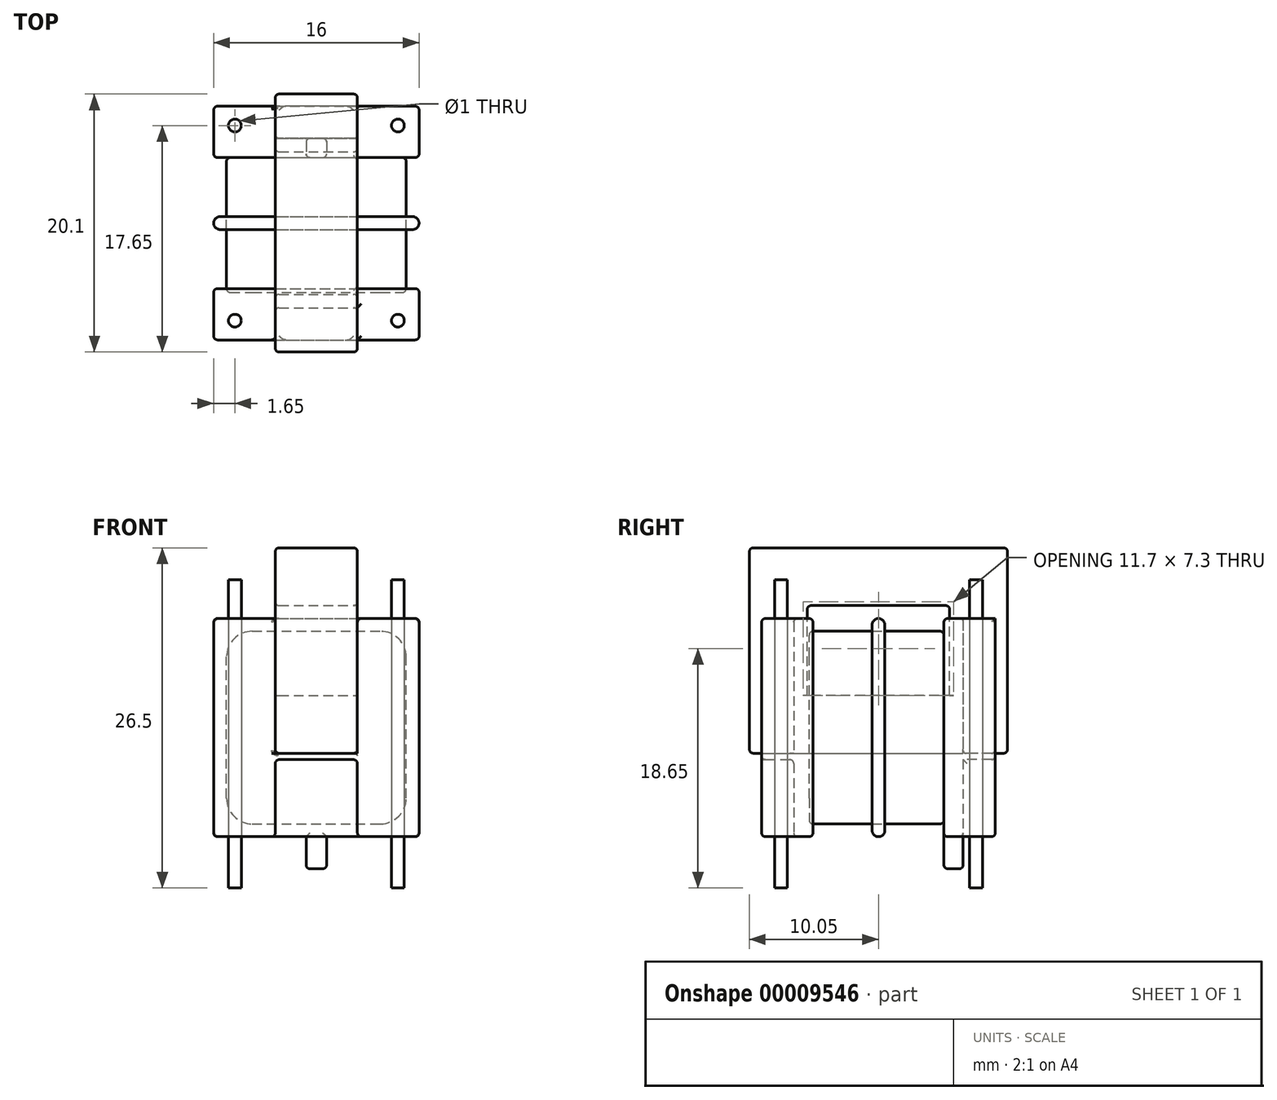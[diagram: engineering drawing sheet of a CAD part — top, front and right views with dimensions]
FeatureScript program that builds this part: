
annotation { "Feature Type Name" : "Feature", "Feature Type Description" : "" }
export const myFeature = defineFeature(function(context is Context, id is Id, definition is map)
    precondition{}
    {
        {
            var Q0;
            Q0=qCreatedBy(makeId("Top.planeOp"),FACE);
            var sketch = newSketch(context, id + "F0", { "sketchPlane" : qUnion([Q0])});
            skCircle(sketch, "E0", {"center": v(-6.35, 7.6) * mm, "radius": 0.5 * mm});
            skCircle(sketch, "E1.0.MirrorC", {"center": v(-6.35, -7.6) * mm, "radius": 0.5 * mm});
            skCircle(sketch, "E2.0.MirrorC", {"center": v(6.35, -7.6) * mm, "radius": 0.5 * mm});
            skCircle(sketch, "E3.0.MirrorC", {"center": v(6.35, 7.6) * mm, "radius": 0.5 * mm});
            skLineSegment(sketch, "E4", {"start": v(-6.35, -7.6) * mm, "end": v(-6.35, 7.6) * mm, "construction": true});
            skLineSegment(sketch, "E5", {"start": v(-6.35, 7.6) * mm, "end": v(6.35, 7.6) * mm, "construction": true});
            skLineSegment(sketch, "E6", {"start": v(6.36, 7.65) * mm, "end": v(6.35, -7.6) * mm, "construction": true});
            skLineSegment(sketch, "E7", {"start": v(-6.35, -7.6) * mm, "end": v(6.35, -7.6) * mm, "construction": true});
            skSolve(sketch);
        }
        {
            var Q0;
            Q0 = qSketchRegion(id + "F0", true);
            extrude(context, id + "F1", {"entities" : qUnion([Q0]), "oppositeDirection" : true, "depth" : 4 * mm});
        }
        {
            var Q0;
            Q0=makeQuery(id+"F0.imprint","IMPRINT",FACE,{"disambiguationData":[TD([[makeQuery(id+"F0.imprint","IMPRINT",EDGE,{"derivedFrom":sQuery(id+"F0.wireOp",EDGE,"E0")}),1.0]])]});
            var sketch = newSketch(context, id + "F2", { "sketchPlane" : qUnion([Q0])});
            skLineSegment(sketch, "E8", {"start": v(0, 0) * mm, "end": v(0, 9.1) * mm, "construction": true});
            skLineSegment(sketch, "E9", {"start": v(0, 0) * mm, "end": v(8, 0) * mm, "construction": true});
            skLineSegment(sketch, "E10.rect.bottom", {"start": v(8, 9.1) * mm, "end": v(-8, 9.1) * mm, "construction": true});
            skLineSegment(sketch, "E10.rect.top", {"start": v(8, -9.1) * mm, "end": v(-8, -9.1) * mm, "construction": true});
            skLineSegment(sketch, "E10.rect.left", {"start": v(8, 9.1) * mm, "end": v(8, -9.1) * mm, "construction": true});
            skLineSegment(sketch, "E10.rect.right", {"start": v(-8, 9.1) * mm, "end": v(-8, -9.1) * mm, "construction": true});
            skPoint(sketch, "E10.rect.middle", {"position": v(0, 0) * mm});
            skLineSegment(sketch, "E11", {"start": v(-8, 5.1) * mm, "end": v(8, 5.1) * mm, "construction": true});
            skLineSegment(sketch, "E12", {"start": v(-3.2, 5.1) * mm, "end": v(-3.2, 9.1) * mm, "construction": true});
            skLineSegment(sketch, "E13.0.MirrorCS", {"start": v(3.2, 5.1) * mm, "end": v(3.2, 9.1) * mm, "construction": true});
            skLineSegment(sketch, "E14", {"start": v(-3.2, 6.6) * mm, "end": v(3.2, 6.6) * mm, "construction": true});
            skLineSegment(sketch, "E15", {"start": v(-8, 5.1) * mm, "end": v(-8, 9.1) * mm});
            skLineSegment(sketch, "E16", {"start": v(-3.2, 9.1) * mm, "end": v(-3.2, 6.6) * mm});
            skLineSegment(sketch, "E17", {"start": v(-8, 9.1) * mm, "end": v(-3.2, 9.1) * mm});
            skLineSegment(sketch, "E18", {"start": v(-3.2, 6.6) * mm, "end": v(3.2, 6.6) * mm});
            skLineSegment(sketch, "E19", {"start": v(3.2, 9.1) * mm, "end": v(3.2, 6.6) * mm});
            skLineSegment(sketch, "E20", {"start": v(3.2, 9.1) * mm, "end": v(8, 9.1) * mm});
            skLineSegment(sketch, "E21", {"start": v(8, 9.1) * mm, "end": v(8, 5.1) * mm});
            skLineSegment(sketch, "E22", {"start": v(-8, 5.1) * mm, "end": v(8, 5.1) * mm});
            skLineSegment(sketch, "E23.0.MirrorCS", {"start": v(-8, -5.1) * mm, "end": v(-8, -9.1) * mm});
            skLineSegment(sketch, "E24.0.MirrorCS", {"start": v(-8, -9.1) * mm, "end": v(-3.2, -9.1) * mm});
            skLineSegment(sketch, "E25.0.MirrorCS", {"start": v(-3.2, -9.1) * mm, "end": v(-3.2, -6.6) * mm});
            skLineSegment(sketch, "E26.0.MirrorCS", {"start": v(-8, -5.1) * mm, "end": v(8, -5.1) * mm});
            skLineSegment(sketch, "E27.0.MirrorCS", {"start": v(-3.2, -6.6) * mm, "end": v(3.2, -6.6) * mm});
            skLineSegment(sketch, "E28.0.MirrorCS", {"start": v(3.2, -9.1) * mm, "end": v(3.2, -6.6) * mm});
            skLineSegment(sketch, "E29.0.MirrorCS", {"start": v(3.2, -9.1) * mm, "end": v(8, -9.1) * mm});
            skLineSegment(sketch, "E30.0.MirrorCS", {"start": v(8, -9.1) * mm, "end": v(8, -5.1) * mm});
            skLineSegment(sketch, "E31", {"start": v(-8, 0.5) * mm, "end": v(8, 0.5) * mm});
            skLineSegment(sketch, "E32.0.MirrorCS", {"start": v(-8, -0.5) * mm, "end": v(8, -0.5) * mm});
            skLineSegment(sketch, "E33", {"start": v(-8, 0.5) * mm, "end": v(-8, -0.5) * mm});
            skLineSegment(sketch, "E34", {"start": v(8, 0.5) * mm, "end": v(8, -0.5) * mm});
            skLineSegment(sketch, "E35", {"start": v(-0.8, 6.6) * mm, "end": v(-0.8, 5.1) * mm});
            skLineSegment(sketch, "E36.0.MirrorCS", {"start": v(0.8, 6.6) * mm, "end": v(0.8, 5.1) * mm});
            skSolve(sketch);
        }
        {
            var Q0;
            Q0=makeQuery(id+"F2.imprint","IMPRINT",FACE,{"disambiguationData":[TD([[makeQuery(id+"F2.imprint","IMPRINT",EDGE,{"derivedFrom":sQuery(id+"F2.wireOp",EDGE,"E15")}),-1.0]])]});
            var Q1;
            Q1=makeQuery(id+"F2.imprint","IMPRINT",FACE,{"disambiguationData":[TD([[makeQuery(id+"F2.imprint","IMPRINT",EDGE,{"derivedFrom":sQuery(id+"F2.wireOp",EDGE,"E23.0.MirrorCS")}),1.0]])]});
            var Q2;
            Q2=makeQuery(id+"F2.imprint","IMPRINT",FACE,{"disambiguationData":[TD([[makeQuery(id+"F2.imprint","IMPRINT",EDGE,{"derivedFrom":sQuery(id+"F2.wireOp",EDGE,"E31")}),-1.0]])]});
            var Q3;
            {var subQ1=sQuery(id+"F2.wireOp",EDGE,"E35");Q3=makeQuery(id+"F2.imprint","IMPRINT",FACE,{"disambiguationData":[TD([[makeQuery(id+"F2.imprint","IMPRINT",EDGE,{"derivedFrom":subQ1}),1.0]])]});}
            var Q4;
            {var subQ3=sQuery(id+"F2.wireOp",EDGE,"E19");Q4=makeQuery(id+"F2.imprint","IMPRINT",FACE,{"disambiguationData":[TD([[makeQuery(id+"F2.imprint","IMPRINT",EDGE,{"derivedFrom":subQ3}),1.0]])]});}
            extrude(context, id + "F3", {"entities" : qUnion([Q0, Q1, Q2, Q3, Q4]), "depth" : 17 * mm});
        }
        {
            var Q0;
            {var subQ1=sQuery(id+"F2.wireOp",EDGE,"E35");Q0=makeQuery(id+"F2.imprint","IMPRINT",FACE,{"disambiguationData":[TD([[makeQuery(id+"F2.imprint","IMPRINT",EDGE,{"derivedFrom":subQ1}),1.0]])]});}
            extrude(context, id + "F4", {"entities" : qUnion([Q0]), "operationType" : NewBodyOperationType.ADD, "oppositeDirection" : true, "depth" : 2.5 * mm});
        }
        {
            var Q0;
            {var subQ0=sQuery(id+"F2.wireOp",EDGE,"E18");Q0=makeQuery(id+"F4.boolean.opBoolean","MERGE",FACE,{"derivedFrom":[makeQuery(id+"F3.opExtrude","SWEPT_FACE",FACE,{"disambiguationData":[OSD([subQ0])]}),makeQuery(id+"F4.opExtrude","SWEPT_FACE",FACE,{"disambiguationData":[OSD([subQ0])]})]});}
            var sketch = newSketch(context, id + "F5", { "sketchPlane" : qUnion([Q0])});
            skLineSegment(sketch, "E37", {"start": v(0, 0) * mm, "end": v(0, 6) * mm, "construction": true});
            skLineSegment(sketch, "E38", {"start": v(-3.2, 6) * mm, "end": v(3.2, 6) * mm});
            skLineSegment(sketch, "E39", {"start": v(-3.2, 6.5) * mm, "end": v(3.2, 6.5) * mm});
            skLineSegment(sketch, "E40", {"start": v(-3.2, 6.5) * mm, "end": v(-3.2, 6) * mm});
            skLineSegment(sketch, "E41", {"start": v(3.2, 6.5) * mm, "end": v(3.2, 6) * mm});
            skSolve(sketch);
        }
        {
            var Q0;
            Q0 = qSketchRegion(id + "F5", true);
            extrude(context, id + "F6", {"entities" : qUnion([Q0]), "operationType" : NewBodyOperationType.ADD, "depth" : 2.5 * mm});
        }
        {
            var Q0;
            Q0=makeQuery(id+"F3.opExtrude","SWEPT_FACE",FACE,{"disambiguationData":[OSD([sQuery(id+"F2.wireOp",EDGE,"E27.0.MirrorCS")])]});
            var sketch = newSketch(context, id + "F7", { "sketchPlane" : qUnion([Q0])});
            skLineSegment(sketch, "E42", {"start": v(-3.2, 6) * mm, "end": v(3.2, 6) * mm});
            skLineSegment(sketch, "E43", {"start": v(-3.2, 6.5) * mm, "end": v(3.2, 6.5) * mm});
            skLineSegment(sketch, "E44", {"start": v(3.2, 6.5) * mm, "end": v(3.2, 6) * mm});
            skLineSegment(sketch, "E45", {"start": v(-3.2, 6) * mm, "end": v(-3.2, 6.5) * mm});
            skSolve(sketch);
        }
        {
            var Q0;
            Q0=makeQuery(id+"F7.imprint","IMPRINT",FACE,{"disambiguationData":[TD([[makeQuery(id+"F7.imprint","IMPRINT",EDGE,{"derivedFrom":sQuery(id+"F7.wireOp",EDGE,"E42")}),1.0]])]});
            extrude(context, id + "F8", {"entities" : qUnion([Q0]), "operationType" : NewBodyOperationType.ADD, "depth" : 2.5 * mm});
        }
        {
            var Q0;
            {var subQ0=sQuery(id+"F2.wireOp",EDGE,"E19");var subQ1=sQuery(id+"F5.wireOp",EDGE,"E39");Q0=makeQuery(id+"F6.boolean.opBoolean","SPLIT",FACE,{"disambiguationData":[TD([makeQuery(id+"F6.opExtrude","SWEPT_FACE",FACE,{"disambiguationData":[OSD([subQ1])]})])],"derivedFrom":makeQuery(id+"F3.opExtrude","SWEPT_FACE",FACE,{"disambiguationData":[OSD([subQ0])]})});}
            var sketch = newSketch(context, id + "F9", { "sketchPlane" : qUnion([Q0])});
            skLineSegment(sketch, "E46", {"start": v(0, 6.5) * mm, "end": v(-10.05, 6.5) * mm});
            skLineSegment(sketch, "E47", {"start": v(-10.05, 6.5) * mm, "end": v(-10.05, 22.5) * mm});
            skLineSegment(sketch, "E48", {"start": v(-10.05, 22.5) * mm, "end": v(0, 22.5) * mm});
            skLineSegment(sketch, "E49.0.MirrorCS", {"start": v(10.05, 6.5) * mm, "end": v(10.05, 22.5) * mm});
            skLineSegment(sketch, "E49.1.MirrorCS", {"start": v(0, 6.5) * mm, "end": v(10.05, 6.5) * mm});
            skLineSegment(sketch, "E49.2.MirrorCS", {"start": v(10.05, 22.5) * mm, "end": v(0, 22.5) * mm});
            skLineSegment(sketch, "E50.0", {"start": v(-5.55, 18) * mm, "end": v(0, 18) * mm});
            skLineSegment(sketch, "E50.1", {"start": v(-5.55, 11) * mm, "end": v(-5.55, 18) * mm});
            skLineSegment(sketch, "E50.2", {"start": v(0, 11) * mm, "end": v(-5.55, 11) * mm});
            skLineSegment(sketch, "E50.3", {"start": v(0, 11) * mm, "end": v(5.55, 11) * mm});
            skLineSegment(sketch, "E50.4", {"start": v(5.55, 11) * mm, "end": v(5.55, 18) * mm});
            skLineSegment(sketch, "E50.5", {"start": v(5.55, 18) * mm, "end": v(0, 18) * mm});
            skSolve(sketch);
        }
        {
            var Q0;
            {var subQ11=sQuery(id+"F9.wireOp",EDGE,"E47");Q0=makeQuery(id+"F9.imprint","IMPRINT",FACE,{"disambiguationData":[TD([[makeQuery(id+"F9.imprint","IMPRINT",EDGE,{"derivedFrom":subQ11}),-1.0]])]});}
            extrude(context, id + "F10", {"entities" : qUnion([Q0]), "depth" : 6.4 * mm});
        }
        {
            var Q0;
            {var subQ0=sQuery(id+"F2.wireOp",EDGE,"E22");Q0=makeQuery(id+"F4.boolean.opBoolean","MERGE",FACE,{"derivedFrom":[makeQuery(id+"F3.opExtrude","SWEPT_FACE",FACE,{"disambiguationData":[OSD([subQ0])]}),makeQuery(id+"F4.opExtrude","SWEPT_FACE",FACE,{"disambiguationData":[OSD([subQ0])]})]});}
            var sketch = newSketch(context, id + "F11", { "sketchPlane" : qUnion([Q0])});
            skLineSegment(sketch, "E51.0", {"start": v(-7, 3) * mm, "end": v(-7, 14) * mm});
            skLineSegment(sketch, "E51.1", {"start": v(-5, 1) * mm, "end": v(5, 1) * mm});
            skLineSegment(sketch, "E51.2", {"start": v(7, 3) * mm, "end": v(7, 14) * mm});
            skLineSegment(sketch, "E51.3", {"start": v(-5, 16) * mm, "end": v(5, 16) * mm});
            skPoint(sketch, "E52.visualSharp", {"position": v(-7, 16) * mm});
            skArc(sketch, "E52.filletArc", {"start": v(-5, 16) * mm, "mid": v(-6.41, 15.41) * mm, "end": v(-7, 14) * mm});
            skPoint(sketch, "E53.visualSharp", {"position": v(7, 16) * mm});
            skArc(sketch, "E53.filletArc", {"start": v(7, 14) * mm, "mid": v(6.41, 15.41) * mm, "end": v(5, 16) * mm});
            skPoint(sketch, "E54.visualSharp", {"position": v(7, 1) * mm});
            skArc(sketch, "E54.filletArc", {"start": v(5, 1) * mm, "mid": v(6.41, 1.59) * mm, "end": v(7, 3) * mm});
            skPoint(sketch, "E55.visualSharp", {"position": v(-7, 1) * mm});
            skArc(sketch, "E55.filletArc", {"start": v(-7, 3) * mm, "mid": v(-6.41, 1.59) * mm, "end": v(-5, 1) * mm});
            skPoint(sketch, "E56.visualSharp", {"position": v(-8, 0) * mm});
            skSolve(sketch);
        }
        {
            var Q0;
            Q0=makeQuery(id+"F11.imprint","IMPRINT",FACE,{"disambiguationData":[TD([[makeQuery(id+"F11.imprint","IMPRINT",EDGE,{"derivedFrom":sQuery(id+"F11.wireOp",EDGE,"E51.0")}),-1.0]])]});
            extrude(context, id + "F12", {"entities" : qUnion([Q0]), "depth" : 10.5 * mm});
        }
        {
            var Q0;
            Q0=makeQuery(id+"F12.opExtrude","SWEPT_FACE",FACE,{"disambiguationData":[OSD([sQuery(id+"F11.wireOp",EDGE,"E51.0")])]});
            var Q1;
            Q1=makeQuery(id+"F3.opExtrude","SWEPT_EDGE",EDGE,{"disambiguationData":[OSD([sQuery(id+"F2.wireOp",EDGE,"E29.0.MirrorCS"),sQuery(id+"F2.wireOp",EDGE,"E30.0.MirrorCS")])]});
            var Q2;
            Q2=makeQuery(id+"F3.opExtrude","CAP_EDGE",EDGE,{"disambiguationData":[OSD([sQuery(id+"F2.wireOp",EDGE,"E29.0.MirrorCS")])],"isStart":false});
            var Q3;
            Q3=makeQuery(id+"F3.opExtrude","CAP_EDGE",EDGE,{"disambiguationData":[OSD([sQuery(id+"F2.wireOp",EDGE,"E30.0.MirrorCS")])],"isStart":false});
            var Q4;
            Q4=makeQuery(id+"F3.opExtrude","SWEPT_EDGE",EDGE,{"disambiguationData":[OSD([sQuery(id+"F2.wireOp",EDGE,"E26.0.MirrorCS"),sQuery(id+"F2.wireOp",EDGE,"E30.0.MirrorCS")])]});
            var Q5;
            Q5=makeQuery(id+"F3.opExtrude","CAP_EDGE",EDGE,{"disambiguationData":[OSD([sQuery(id+"F2.wireOp",EDGE,"E26.0.MirrorCS")])],"isStart":false});
            var Q6;
            {var subQ0=sQuery(id+"F2.wireOp",EDGE,"E28.0.MirrorCS");var subQ1=sQuery(id+"F2.wireOp",EDGE,"E29.0.MirrorCS");var subQ2=sQuery(id+"F7.wireOp",EDGE,"E42");Q6=makeQuery(id+"F8.boolean.opBoolean","SPLIT",EDGE,{"disambiguationData":[TD([makeQuery(id+"F8.opExtrude","SWEPT_FACE",FACE,{"disambiguationData":[OSD([subQ2])]})])],"derivedFrom":makeQuery(id+"F3.opExtrude","SWEPT_EDGE",EDGE,{"disambiguationData":[OSD([subQ0,subQ1])]})});}
            var Q7;
            Q7=makeQuery(id+"F3.opExtrude","CAP_EDGE",EDGE,{"disambiguationData":[OSD([sQuery(id+"F2.wireOp",EDGE,"E29.0.MirrorCS")])],"isStart":true});
            var Q8;
            {var subQ0=sQuery(id+"F2.wireOp",EDGE,"E24.0.MirrorCS");var subQ1=sQuery(id+"F2.wireOp",EDGE,"E25.0.MirrorCS");var subQ2=sQuery(id+"F7.wireOp",EDGE,"E43");Q8=makeQuery(id+"F8.boolean.opBoolean","SPLIT",EDGE,{"disambiguationData":[TD([makeQuery(id+"F8.opExtrude","SWEPT_FACE",FACE,{"disambiguationData":[OSD([subQ2])]})])],"derivedFrom":makeQuery(id+"F3.opExtrude","SWEPT_EDGE",EDGE,{"disambiguationData":[OSD([subQ0,subQ1])]})});}
            var Q9;
            Q9=makeQuery(id+"F3.opExtrude","CAP_EDGE",EDGE,{"disambiguationData":[OSD([sQuery(id+"F2.wireOp",EDGE,"E25.0.MirrorCS")])],"isStart":false});
            var Q10;
            Q10=makeQuery(id+"F3.opExtrude","CAP_EDGE",EDGE,{"disambiguationData":[OSD([sQuery(id+"F2.wireOp",EDGE,"E27.0.MirrorCS")])],"isStart":false});
            var Q11;
            Q11=makeQuery(id+"F3.opExtrude","SWEPT_EDGE",EDGE,{"disambiguationData":[OSD([sQuery(id+"F2.wireOp",EDGE,"E23.0.MirrorCS"),sQuery(id+"F2.wireOp",EDGE,"E24.0.MirrorCS")])]});
            var Q12;
            Q12=makeQuery(id+"F3.opExtrude","CAP_EDGE",EDGE,{"disambiguationData":[OSD([sQuery(id+"F2.wireOp",EDGE,"E23.0.MirrorCS")])],"isStart":false});
            var Q13;
            Q13=makeQuery(id+"F3.opExtrude","CAP_EDGE",EDGE,{"disambiguationData":[OSD([sQuery(id+"F2.wireOp",EDGE,"E24.0.MirrorCS")])],"isStart":false});
            var Q14;
            Q14=makeQuery(id+"F3.opExtrude","SWEPT_EDGE",EDGE,{"disambiguationData":[OSD([sQuery(id+"F2.wireOp",EDGE,"E23.0.MirrorCS"),sQuery(id+"F2.wireOp",EDGE,"E26.0.MirrorCS")])]});
            var Q15;
            Q15=makeQuery(id+"F3.opExtrude","CAP_EDGE",EDGE,{"disambiguationData":[OSD([sQuery(id+"F2.wireOp",EDGE,"E23.0.MirrorCS")])],"isStart":true});
            var Q16;
            Q16=makeQuery(id+"F3.opExtrude","CAP_EDGE",EDGE,{"disambiguationData":[OSD([sQuery(id+"F2.wireOp",EDGE,"E26.0.MirrorCS")])],"isStart":true});
            var Q17;
            Q17=makeQuery(id+"F3.opExtrude","CAP_EDGE",EDGE,{"disambiguationData":[OSD([sQuery(id+"F2.wireOp",EDGE,"E27.0.MirrorCS")])],"isStart":true});
            var Q18;
            Q18=makeQuery(id+"F3.opExtrude","CAP_EDGE",EDGE,{"disambiguationData":[OSD([sQuery(id+"F2.wireOp",EDGE,"E25.0.MirrorCS")])],"isStart":true});
            var Q19;
            Q19=makeQuery(id+"F3.opExtrude","CAP_EDGE",EDGE,{"disambiguationData":[OSD([sQuery(id+"F2.wireOp",EDGE,"E24.0.MirrorCS")])],"isStart":true});
            var Q20;
            Q20=makeQuery(id+"F3.opExtrude","CAP_EDGE",EDGE,{"disambiguationData":[OSD([sQuery(id+"F2.wireOp",EDGE,"E28.0.MirrorCS")])],"isStart":true});
            var Q21;
            Q21=makeQuery(id+"F3.opExtrude","CAP_EDGE",EDGE,{"disambiguationData":[OSD([sQuery(id+"F2.wireOp",EDGE,"E30.0.MirrorCS")])],"isStart":true});
            var Q22;
            Q22=makeQuery(id+"F3.opExtrude","CAP_EDGE",EDGE,{"disambiguationData":[OSD([sQuery(id+"F2.wireOp",EDGE,"E28.0.MirrorCS")])],"isStart":false});
            var Q23;
            {var subQ0=sQuery(id+"F2.wireOp",EDGE,"E22");var subQ1=sQuery(id+"F2.wireOp",EDGE,"E21");Q23=makeQuery(id+"F4.boolean.opBoolean","SPLIT",EDGE,{"disambiguationData":[TD([makeQuery(id+"F3.opExtrude","SWEPT_FACE",FACE,{"disambiguationData":[OSD([subQ1])]})])],"derivedFrom":makeQuery(id+"F3.opExtrude","CAP_EDGE",EDGE,{"disambiguationData":[OSD([subQ0])],"isStart":true})});}
            var Q24;
            Q24=makeQuery(id+"F3.opExtrude","CAP_EDGE",EDGE,{"disambiguationData":[OSD([sQuery(id+"F2.wireOp",EDGE,"E21")])],"isStart":true});
            var Q25;
            Q25=makeQuery(id+"F3.opExtrude","CAP_EDGE",EDGE,{"disambiguationData":[OSD([sQuery(id+"F2.wireOp",EDGE,"E20")])],"isStart":true});
            var Q26;
            Q26=makeQuery(id+"F3.opExtrude","CAP_EDGE",EDGE,{"disambiguationData":[OSD([sQuery(id+"F2.wireOp",EDGE,"E19")])],"isStart":true});
            var Q27;
            {var subQ0=sQuery(id+"F2.wireOp",EDGE,"E18");var subQ1=sQuery(id+"F2.wireOp",EDGE,"E19");Q27=makeQuery(id+"F4.boolean.opBoolean","SPLIT",EDGE,{"disambiguationData":[TD([makeQuery(id+"F3.opExtrude","SWEPT_FACE",FACE,{"disambiguationData":[OSD([subQ1])]})])],"derivedFrom":makeQuery(id+"F3.opExtrude","CAP_EDGE",EDGE,{"disambiguationData":[OSD([subQ0])],"isStart":true})});}
            var Q28;
            Q28=makeQuery(id+"F4.opExtrude","SWEPT_EDGE",EDGE,{"disambiguationData":[OSD([sQuery(id+"F2.wireOp",EDGE,"E18"),sQuery(id+"F2.wireOp",EDGE,"E36.0.MirrorCS")])]});
            var Q29;
            Q29=makeQuery(id+"F4.opExtrude","CAP_EDGE",EDGE,{"disambiguationData":[OSD([sQuery(id+"F2.wireOp",EDGE,"E18")])],"isStart":false});
            var Q30;
            Q30=makeQuery(id+"F4.opExtrude","SWEPT_EDGE",EDGE,{"disambiguationData":[OSD([sQuery(id+"F2.wireOp",EDGE,"E18"),sQuery(id+"F2.wireOp",EDGE,"E35")])]});
            var Q31;
            {var subQ0=sQuery(id+"F2.wireOp",EDGE,"E18");var subQ1=sQuery(id+"F2.wireOp",EDGE,"E16");Q31=makeQuery(id+"F4.boolean.opBoolean","SPLIT",EDGE,{"disambiguationData":[TD([makeQuery(id+"F3.opExtrude","SWEPT_FACE",FACE,{"disambiguationData":[OSD([subQ1])]})])],"derivedFrom":makeQuery(id+"F3.opExtrude","CAP_EDGE",EDGE,{"disambiguationData":[OSD([subQ0])],"isStart":true})});}
            var Q32;
            {var subQ0=sQuery(id+"F2.wireOp",EDGE,"E18");var subQ1=sQuery(id+"F2.wireOp",EDGE,"E16");Q32=makeQuery(id+"F4.boolean.opBoolean","SPLIT",EDGE,{"disambiguationData":[TD([makeQuery(id+"F3.opExtrude","SWEPT_FACE",FACE,{"disambiguationData":[OSD([subQ1])]})])],"derivedFrom":makeQuery(id+"F3.opExtrude","CAP_EDGE",EDGE,{"disambiguationData":[OSD([subQ0])],"isStart":true})});}
            var Q33;
            Q33=makeQuery(id+"F3.opExtrude","CAP_EDGE",EDGE,{"disambiguationData":[OSD([sQuery(id+"F2.wireOp",EDGE,"E16")])],"isStart":true});
            var Q34;
            Q34=makeQuery(id+"F3.opExtrude","CAP_EDGE",EDGE,{"disambiguationData":[OSD([sQuery(id+"F2.wireOp",EDGE,"E17")])],"isStart":true});
            var Q35;
            Q35=makeQuery(id+"F3.opExtrude","CAP_EDGE",EDGE,{"disambiguationData":[OSD([sQuery(id+"F2.wireOp",EDGE,"E15")])],"isStart":true});
            var Q36;
            {var subQ0=sQuery(id+"F2.wireOp",EDGE,"E22");var subQ1=sQuery(id+"F2.wireOp",EDGE,"E15");Q36=makeQuery(id+"F4.boolean.opBoolean","SPLIT",EDGE,{"disambiguationData":[TD([makeQuery(id+"F3.opExtrude","SWEPT_FACE",FACE,{"disambiguationData":[OSD([subQ1])]})])],"derivedFrom":makeQuery(id+"F3.opExtrude","CAP_EDGE",EDGE,{"disambiguationData":[OSD([subQ0])],"isStart":true})});}
            var Q37;
            Q37=makeQuery(id+"F4.opExtrude","SWEPT_EDGE",EDGE,{"disambiguationData":[OSD([sQuery(id+"F2.wireOp",EDGE,"E22"),sQuery(id+"F2.wireOp",EDGE,"E35")])]});
            var Q38;
            Q38=makeQuery(id+"F4.opExtrude","CAP_EDGE",EDGE,{"disambiguationData":[OSD([sQuery(id+"F2.wireOp",EDGE,"E22")])],"isStart":false});
            var Q39;
            Q39=makeQuery(id+"F4.opExtrude","SWEPT_EDGE",EDGE,{"disambiguationData":[OSD([sQuery(id+"F2.wireOp",EDGE,"E22"),sQuery(id+"F2.wireOp",EDGE,"E36.0.MirrorCS")])]});
            var Q40;
            Q40=makeQuery(id+"F4.opExtrude","CAP_EDGE",EDGE,{"disambiguationData":[OSD([sQuery(id+"F2.wireOp",EDGE,"E35")])],"isStart":false});
            var Q41;
            Q41=makeQuery(id+"F4.opExtrude","CAP_EDGE",EDGE,{"disambiguationData":[OSD([sQuery(id+"F2.wireOp",EDGE,"E36.0.MirrorCS")])],"isStart":false});
            var Q42;
            {var subQ0=sQuery(id+"F2.wireOp",EDGE,"E16");var subQ1=sQuery(id+"F2.wireOp",EDGE,"E18");Q42=makeQuery(id+"F6.boolean.opBoolean","SPLIT",EDGE,{"disambiguationData":[TD([makeQuery(id+"F6.opExtrude","SWEPT_FACE",FACE,{"disambiguationData":[OSD([sQuery(id+"F5.wireOp",EDGE,"E38")])]})])],"derivedFrom":makeQuery(id+"F3.opExtrude","SWEPT_EDGE",EDGE,{"disambiguationData":[OSD([subQ0,subQ1])]})});}
            var Q43;
            {var subQ0=sQuery(id+"F2.wireOp",EDGE,"E16");var subQ1=sQuery(id+"F2.wireOp",EDGE,"E17");var subQ2=sQuery(id+"F5.wireOp",EDGE,"E38");Q43=makeQuery(id+"F6.boolean.opBoolean","SPLIT",EDGE,{"disambiguationData":[TD([makeQuery(id+"F6.opExtrude","SWEPT_FACE",FACE,{"disambiguationData":[OSD([subQ2])]})])],"derivedFrom":makeQuery(id+"F3.opExtrude","SWEPT_EDGE",EDGE,{"disambiguationData":[OSD([subQ0,subQ1])]})});}
            var Q44;
            Q44=makeQuery(id+"F6.opExtrude","CAP_EDGE",EDGE,{"disambiguationData":[OSD([sQuery(id+"F5.wireOp",EDGE,"E38")])],"isStart":true});
            var Q45;
            Q45=makeQuery(id+"F6.opExtrude","SWEPT_EDGE",EDGE,{"disambiguationData":[OSD([sQuery(id+"F2.wireOp",EDGE,"E16"),sQuery(id+"F2.wireOp",EDGE,"E18"),sQuery(id+"F5.wireOp",EDGE,"E38"),sQuery(id+"F5.wireOp",EDGE,"E41")])]});
            var Q46;
            {var subQ0=sQuery(id+"F2.wireOp",EDGE,"E18");var subQ1=sQuery(id+"F2.wireOp",EDGE,"E19");Q46=makeQuery(id+"F6.boolean.opBoolean","SPLIT",EDGE,{"disambiguationData":[TD([makeQuery(id+"F6.opExtrude","SWEPT_FACE",FACE,{"disambiguationData":[OSD([sQuery(id+"F5.wireOp",EDGE,"E38")])]})])],"derivedFrom":makeQuery(id+"F3.opExtrude","SWEPT_EDGE",EDGE,{"disambiguationData":[OSD([subQ0,subQ1])]})});}
            var Q47;
            {var subQ0=sQuery(id+"F2.wireOp",EDGE,"E19");var subQ1=sQuery(id+"F2.wireOp",EDGE,"E20");var subQ2=sQuery(id+"F5.wireOp",EDGE,"E38");Q47=makeQuery(id+"F6.boolean.opBoolean","SPLIT",EDGE,{"disambiguationData":[TD([makeQuery(id+"F6.opExtrude","SWEPT_FACE",FACE,{"disambiguationData":[OSD([subQ2])]})])],"derivedFrom":makeQuery(id+"F3.opExtrude","SWEPT_EDGE",EDGE,{"disambiguationData":[OSD([subQ0,subQ1])]})});}
            var Q48;
            Q48=makeQuery(id+"F6.opExtrude","SWEPT_EDGE",EDGE,{"disambiguationData":[OSD([sQuery(id+"F2.wireOp",EDGE,"E18"),sQuery(id+"F2.wireOp",EDGE,"E19"),sQuery(id+"F5.wireOp",EDGE,"E38"),sQuery(id+"F5.wireOp",EDGE,"E40")])]});
            var Q49;
            Q49=makeQuery(id+"F3.opExtrude","SWEPT_EDGE",EDGE,{"disambiguationData":[OSD([sQuery(id+"F2.wireOp",EDGE,"E20"),sQuery(id+"F2.wireOp",EDGE,"E21")])]});
            var Q50;
            Q50=makeQuery(id+"F3.opExtrude","SWEPT_EDGE",EDGE,{"disambiguationData":[OSD([sQuery(id+"F2.wireOp",EDGE,"E21"),sQuery(id+"F2.wireOp",EDGE,"E22")])]});
            var Q51;
            Q51=makeQuery(id+"F3.opExtrude","CAP_EDGE",EDGE,{"disambiguationData":[OSD([sQuery(id+"F2.wireOp",EDGE,"E21")])],"isStart":false});
            var Q52;
            Q52=makeQuery(id+"F3.opExtrude","CAP_EDGE",EDGE,{"disambiguationData":[OSD([sQuery(id+"F2.wireOp",EDGE,"E20")])],"isStart":false});
            var Q53;
            Q53=makeQuery(id+"F3.opExtrude","CAP_EDGE",EDGE,{"disambiguationData":[OSD([sQuery(id+"F2.wireOp",EDGE,"E22")])],"isStart":false});
            var Q54;
            {var subQ0=sQuery(id+"F2.wireOp",EDGE,"E24.0.MirrorCS");var subQ1=sQuery(id+"F2.wireOp",EDGE,"E25.0.MirrorCS");var subQ2=sQuery(id+"F7.wireOp",EDGE,"E42");Q54=makeQuery(id+"F8.boolean.opBoolean","SPLIT",EDGE,{"disambiguationData":[TD([makeQuery(id+"F8.opExtrude","SWEPT_FACE",FACE,{"disambiguationData":[OSD([subQ2])]})])],"derivedFrom":makeQuery(id+"F3.opExtrude","SWEPT_EDGE",EDGE,{"disambiguationData":[OSD([subQ0,subQ1])]})});}
            var Q55;
            {var subQ0=sQuery(id+"F2.wireOp",EDGE,"E25.0.MirrorCS");var subQ1=sQuery(id+"F2.wireOp",EDGE,"E27.0.MirrorCS");Q55=makeQuery(id+"F8.boolean.opBoolean","SPLIT",EDGE,{"disambiguationData":[TD([makeQuery(id+"F8.opExtrude","SWEPT_FACE",FACE,{"disambiguationData":[OSD([sQuery(id+"F7.wireOp",EDGE,"E42")])]})])],"derivedFrom":makeQuery(id+"F3.opExtrude","SWEPT_EDGE",EDGE,{"disambiguationData":[OSD([subQ0,subQ1])]})});}
            var Q56;
            Q56=makeQuery(id+"F8.opExtrude","SWEPT_EDGE",EDGE,{"disambiguationData":[OSD([sQuery(id+"F2.wireOp",EDGE,"E25.0.MirrorCS"),sQuery(id+"F2.wireOp",EDGE,"E27.0.MirrorCS"),sQuery(id+"F7.wireOp",EDGE,"E42"),sQuery(id+"F7.wireOp",EDGE,"E45")])]});
            var Q57;
            Q57=makeQuery(id+"F8.opExtrude","CAP_EDGE",EDGE,{"disambiguationData":[OSD([sQuery(id+"F7.wireOp",EDGE,"E42")])],"isStart":true});
            var Q58;
            Q58=makeQuery(id+"F8.opExtrude","SWEPT_EDGE",EDGE,{"disambiguationData":[OSD([sQuery(id+"F2.wireOp",EDGE,"E27.0.MirrorCS"),sQuery(id+"F2.wireOp",EDGE,"E28.0.MirrorCS"),sQuery(id+"F7.wireOp",EDGE,"E42"),sQuery(id+"F7.wireOp",EDGE,"E44")])]});
            var Q59;
            {var subQ0=sQuery(id+"F2.wireOp",EDGE,"E27.0.MirrorCS");var subQ1=sQuery(id+"F2.wireOp",EDGE,"E28.0.MirrorCS");Q59=makeQuery(id+"F8.boolean.opBoolean","SPLIT",EDGE,{"disambiguationData":[TD([makeQuery(id+"F8.opExtrude","SWEPT_FACE",FACE,{"disambiguationData":[OSD([sQuery(id+"F7.wireOp",EDGE,"E42")])]})])],"derivedFrom":makeQuery(id+"F3.opExtrude","SWEPT_EDGE",EDGE,{"disambiguationData":[OSD([subQ0,subQ1])]})});}
            var Q60;
            {var subQ0=sQuery(id+"F2.wireOp",EDGE,"E25.0.MirrorCS");var subQ1=sQuery(id+"F2.wireOp",EDGE,"E27.0.MirrorCS");Q60=makeQuery(id+"F8.boolean.opBoolean","SPLIT",EDGE,{"disambiguationData":[TD([makeQuery(id+"F8.opExtrude","SWEPT_FACE",FACE,{"disambiguationData":[OSD([sQuery(id+"F7.wireOp",EDGE,"E43")])]})])],"derivedFrom":makeQuery(id+"F3.opExtrude","SWEPT_EDGE",EDGE,{"disambiguationData":[OSD([subQ0,subQ1])]})});}
            var Q61;
            Q61=makeQuery(id+"F3.opExtrude","SWEPT_EDGE",EDGE,{"disambiguationData":[OSD([sQuery(id+"F2.wireOp",EDGE,"E15"),sQuery(id+"F2.wireOp",EDGE,"E22")])]});
            var Q62;
            Q62=makeQuery(id+"F3.opExtrude","CAP_EDGE",EDGE,{"disambiguationData":[OSD([sQuery(id+"F2.wireOp",EDGE,"E15")])],"isStart":false});
            var Q63;
            Q63=makeQuery(id+"F3.opExtrude","SWEPT_EDGE",EDGE,{"disambiguationData":[OSD([sQuery(id+"F2.wireOp",EDGE,"E15"),sQuery(id+"F2.wireOp",EDGE,"E17")])]});
            var Q64;
            Q64=makeQuery(id+"F3.opExtrude","CAP_EDGE",EDGE,{"disambiguationData":[OSD([sQuery(id+"F2.wireOp",EDGE,"E17")])],"isStart":false});
            var Q65;
            {var subQ0=sQuery(id+"F2.wireOp",EDGE,"E16");var subQ1=sQuery(id+"F2.wireOp",EDGE,"E17");var subQ2=sQuery(id+"F5.wireOp",EDGE,"E39");Q65=makeQuery(id+"F6.boolean.opBoolean","SPLIT",EDGE,{"disambiguationData":[TD([makeQuery(id+"F6.opExtrude","SWEPT_FACE",FACE,{"disambiguationData":[OSD([subQ2])]})])],"derivedFrom":makeQuery(id+"F3.opExtrude","SWEPT_EDGE",EDGE,{"disambiguationData":[OSD([subQ0,subQ1])]})});}
            var Q66;
            {var subQ0=sQuery(id+"F2.wireOp",EDGE,"E16");var subQ1=sQuery(id+"F2.wireOp",EDGE,"E18");Q66=makeQuery(id+"F6.boolean.opBoolean","SPLIT",EDGE,{"disambiguationData":[TD([makeQuery(id+"F6.opExtrude","SWEPT_FACE",FACE,{"disambiguationData":[OSD([sQuery(id+"F5.wireOp",EDGE,"E39")])]})])],"derivedFrom":makeQuery(id+"F3.opExtrude","SWEPT_EDGE",EDGE,{"disambiguationData":[OSD([subQ0,subQ1])]})});}
            fillet(context, id + "F13", {"entities" : qUnion([Q0, Q1, Q2, Q3, Q4, Q5, Q6, Q7, Q8, Q9, Q10, Q11, Q12, Q13, Q14, Q15, Q16, Q17, Q18, Q19, Q20, Q21, Q22, Q23, Q24, Q25, Q26, Q27, Q28, Q29, Q30, Q31, Q32, Q33, Q34, Q35, Q36, Q37, Q38, Q39, Q40, Q41, Q42, Q43, Q44, Q45, Q46, Q47, Q48, Q49, Q50, Q51, Q52, Q53, Q54, Q55, Q56, Q57, Q58, Q59, Q60, Q61, Q62, Q63, Q64, Q65, Q66]), "radius" : 0.3 * mm, "tangentPropagation" : true, "allowEdgeOverflow" : false});
        }
        {
            var Q0;
            Q0=makeQuery(id+"F3.opExtrude","SWEPT_EDGE",EDGE,{"disambiguationData":[OSD([sQuery(id+"F2.wireOp",EDGE,"E31"),sQuery(id+"F2.wireOp",EDGE,"E33")])]});
            var Q1;
            Q1=makeQuery(id+"F3.opExtrude","SWEPT_EDGE",EDGE,{"disambiguationData":[OSD([sQuery(id+"F2.wireOp",EDGE,"E32.0.MirrorCS"),sQuery(id+"F2.wireOp",EDGE,"E33")])]});
            var Q2;
            Q2=makeQuery(id+"F3.opExtrude","CAP_EDGE",EDGE,{"disambiguationData":[OSD([sQuery(id+"F2.wireOp",EDGE,"E31")])],"isStart":true});
            var Q3;
            Q3=makeQuery(id+"F3.opExtrude","CAP_EDGE",EDGE,{"disambiguationData":[OSD([sQuery(id+"F2.wireOp",EDGE,"E32.0.MirrorCS")])],"isStart":true});
            var Q4;
            Q4=makeQuery(id+"F3.opExtrude","SWEPT_EDGE",EDGE,{"disambiguationData":[OSD([sQuery(id+"F2.wireOp",EDGE,"E32.0.MirrorCS"),sQuery(id+"F2.wireOp",EDGE,"E34")])]});
            var Q5;
            Q5=makeQuery(id+"F3.opExtrude","SWEPT_EDGE",EDGE,{"disambiguationData":[OSD([sQuery(id+"F2.wireOp",EDGE,"E31"),sQuery(id+"F2.wireOp",EDGE,"E34")])]});
            var Q6;
            Q6=makeQuery(id+"F3.opExtrude","CAP_EDGE",EDGE,{"disambiguationData":[OSD([sQuery(id+"F2.wireOp",EDGE,"E32.0.MirrorCS")])],"isStart":false});
            var Q7;
            Q7=makeQuery(id+"F3.opExtrude","CAP_EDGE",EDGE,{"disambiguationData":[OSD([sQuery(id+"F2.wireOp",EDGE,"E31")])],"isStart":false});
            var Q8;
            Q8=makeQuery(id+"F3.opExtrude","CAP_EDGE",EDGE,{"disambiguationData":[OSD([sQuery(id+"F2.wireOp",EDGE,"E34")])],"isStart":false});
            var Q9;
            Q9=makeQuery(id+"F3.opExtrude","CAP_EDGE",EDGE,{"disambiguationData":[OSD([sQuery(id+"F2.wireOp",EDGE,"E34")])],"isStart":true});
            var Q10;
            Q10=makeQuery(id+"F3.opExtrude","CAP_EDGE",EDGE,{"disambiguationData":[OSD([sQuery(id+"F2.wireOp",EDGE,"E33")])],"isStart":true});
            var Q11;
            Q11=makeQuery(id+"F3.opExtrude","CAP_EDGE",EDGE,{"disambiguationData":[OSD([sQuery(id+"F2.wireOp",EDGE,"E33")])],"isStart":false});
            fillet(context, id + "F14", {"entities" : qUnion([Q0, Q1, Q2, Q3, Q4, Q5, Q6, Q7, Q8, Q9, Q10, Q11]), "radius" : 0.5 * mm, "tangentPropagation" : true, "allowEdgeOverflow" : false});
        }
        {
            var Q0;
            Q0=makeQuery(id+"F6.opExtrude","CAP_EDGE",EDGE,{"disambiguationData":[OSD([sQuery(id+"F5.wireOp",EDGE,"E39")])],"isStart":false});
            var Q1;
            {var subQ0=sQuery(id+"F2.wireOp",EDGE,"E16");var subQ1=sQuery(id+"F2.wireOp",EDGE,"E17");var subQ2=sQuery(id+"F5.wireOp",EDGE,"E39");Q1=makeQuery(id+"F13.opFillet","BLEND_FACE",FACE,{"disambiguationData":[OSD([subQ0,subQ1]),TDD([makeQuery(id+"F6.boolean.opBoolean","SPLIT",EDGE,{"disambiguationData":[TD([makeQuery(id+"F6.opExtrude","SWEPT_FACE",FACE,{"disambiguationData":[OSD([subQ2])]})])],"derivedFrom":makeQuery(id+"F3.opExtrude","SWEPT_EDGE",EDGE,{"disambiguationData":[OSD([subQ0,subQ1])]})})])]});}
            fillet(context, id + "F15", {"entities" : qUnion([Q0, Q1]), "radius" : 0.2 * mm, "tangentPropagation" : true, "allowEdgeOverflow" : false});
        }
        {
            var Q0;
            Q0=makeQuery(id+"F10.opExtrude","CAP_EDGE",EDGE,{"disambiguationData":[OSD([sQuery(id+"F9.wireOp",EDGE,"E47")])],"isStart":true});
            var Q1;
            Q1=makeQuery(id+"F10.opExtrude","CAP_EDGE",EDGE,{"disambiguationData":[OSD([sQuery(id+"F9.wireOp",EDGE,"E46")])],"isStart":true});
            var Q2;
            Q2=makeQuery(id+"F10.opExtrude","SWEPT_EDGE",EDGE,{"disambiguationData":[OSD([sQuery(id+"F9.wireOp",EDGE,"E46"),sQuery(id+"F9.wireOp",EDGE,"E47")])]});
            var Q3;
            Q3=makeQuery(id+"F10.opExtrude","CAP_EDGE",EDGE,{"disambiguationData":[OSD([sQuery(id+"F9.wireOp",EDGE,"E47")])],"isStart":false});
            var Q4;
            Q4=makeQuery(id+"F10.opExtrude","CAP_EDGE",EDGE,{"disambiguationData":[OSD([sQuery(id+"F9.wireOp",EDGE,"E46")])],"isStart":false});
            var Q5;
            Q5=makeQuery(id+"F10.opExtrude","CAP_EDGE",EDGE,{"disambiguationData":[OSD([sQuery(id+"F9.wireOp",EDGE,"E48"),sQuery(id+"F9.wireOp",EDGE,"E49.2.MirrorCS")])],"isStart":false});
            var Q6;
            Q6=makeQuery(id+"F10.opExtrude","CAP_EDGE",EDGE,{"disambiguationData":[OSD([sQuery(id+"F9.wireOp",EDGE,"E48"),sQuery(id+"F9.wireOp",EDGE,"E49.2.MirrorCS")])],"isStart":true});
            var Q7;
            Q7=makeQuery(id+"F10.opExtrude","CAP_EDGE",EDGE,{"disambiguationData":[OSD([sQuery(id+"F9.wireOp",EDGE,"E49.0.MirrorCS")])],"isStart":false});
            var Q8;
            Q8=makeQuery(id+"F10.opExtrude","SWEPT_EDGE",EDGE,{"disambiguationData":[OSD([sQuery(id+"F9.wireOp",EDGE,"E49.0.MirrorCS"),sQuery(id+"F9.wireOp",EDGE,"E49.2.MirrorCS")])]});
            var Q9;
            Q9=makeQuery(id+"F10.opExtrude","CAP_EDGE",EDGE,{"disambiguationData":[OSD([sQuery(id+"F9.wireOp",EDGE,"E49.0.MirrorCS")])],"isStart":true});
            var Q10;
            Q10=makeQuery(id+"F10.opExtrude","SWEPT_EDGE",EDGE,{"disambiguationData":[OSD([sQuery(id+"F9.wireOp",EDGE,"E49.0.MirrorCS"),sQuery(id+"F9.wireOp",EDGE,"E49.1.MirrorCS")])]});
            var Q11;
            Q11=makeQuery(id+"F10.opExtrude","CAP_EDGE",EDGE,{"disambiguationData":[OSD([sQuery(id+"F9.wireOp",EDGE,"E46"),sQuery(id+"F9.wireOp",EDGE,"E49.1.MirrorCS")])],"isStart":false});
            var Q12;
            Q12=makeQuery(id+"F10.opExtrude","CAP_EDGE",EDGE,{"disambiguationData":[OSD([sQuery(id+"F9.wireOp",EDGE,"E46"),sQuery(id+"F9.wireOp",EDGE,"E49.1.MirrorCS")])],"isStart":true});
            var Q13;
            Q13=makeQuery(id+"F10.opExtrude","CAP_EDGE",EDGE,{"disambiguationData":[OSD([sQuery(id+"F9.wireOp",EDGE,"E50.1")])],"isStart":false});
            var Q14;
            Q14=makeQuery(id+"F10.opExtrude","CAP_EDGE",EDGE,{"disambiguationData":[OSD([sQuery(id+"F9.wireOp",EDGE,"E50.0"),sQuery(id+"F9.wireOp",EDGE,"E50.5")])],"isStart":false});
            var Q15;
            Q15=makeQuery(id+"F10.opExtrude","CAP_EDGE",EDGE,{"disambiguationData":[OSD([sQuery(id+"F9.wireOp",EDGE,"E50.4")])],"isStart":false});
            var Q16;
            Q16=makeQuery(id+"F10.opExtrude","SWEPT_EDGE",EDGE,{"disambiguationData":[OSD([sQuery(id+"F9.wireOp",EDGE,"E50.0"),sQuery(id+"F9.wireOp",EDGE,"E50.1")])]});
            var Q17;
            Q17=makeQuery(id+"F10.opExtrude","SWEPT_EDGE",EDGE,{"disambiguationData":[OSD([sQuery(id+"F9.wireOp",EDGE,"E50.4"),sQuery(id+"F9.wireOp",EDGE,"E50.5")])]});
            var Q18;
            Q18=makeQuery(id+"F10.opExtrude","CAP_EDGE",EDGE,{"disambiguationData":[OSD([sQuery(id+"F9.wireOp",EDGE,"E50.4")])],"isStart":true});
            var Q19;
            Q19=makeQuery(id+"F10.opExtrude","CAP_EDGE",EDGE,{"disambiguationData":[OSD([sQuery(id+"F9.wireOp",EDGE,"E50.1")])],"isStart":true});
            var Q20;
            Q20=makeQuery(id+"F10.opExtrude","SWEPT_EDGE",EDGE,{"disambiguationData":[OSD([sQuery(id+"F9.wireOp",EDGE,"E47"),sQuery(id+"F9.wireOp",EDGE,"E48")])]});
            fillet(context, id + "F16", {"entities" : qUnion([Q0, Q1, Q2, Q3, Q4, Q5, Q6, Q7, Q8, Q9, Q10, Q11, Q12, Q13, Q14, Q15, Q16, Q17, Q18, Q19, Q20]), "radius" : 0.3 * mm, "tangentPropagation" : true, "allowEdgeOverflow" : false});
        }
        {
            var Q0;
            Q0 = qSketchRegion(id + "F0", true);
            extrude(context, id + "F17", {"entities" : qUnion([Q0]), "depth" : 20 * mm});
        }
    });
